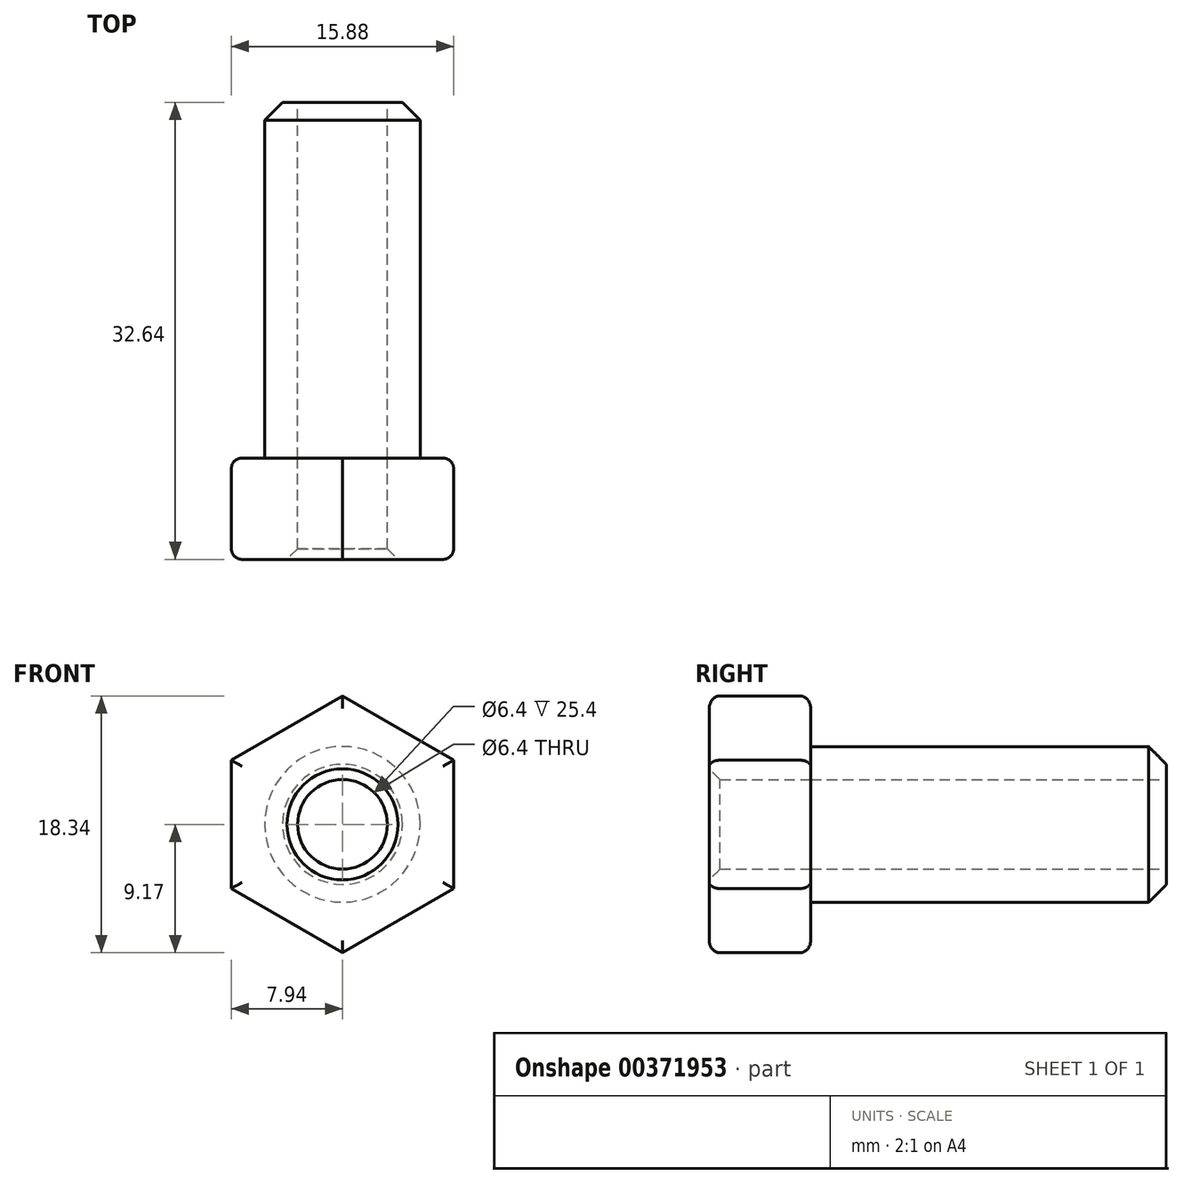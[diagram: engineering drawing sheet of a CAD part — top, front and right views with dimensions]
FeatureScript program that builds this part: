
annotation { "Feature Type Name" : "Feature", "Feature Type Description" : "" }
export const myFeature = defineFeature(function(context is Context, id is Id, definition is map)
    precondition{}
    {
        {
            var Q0;
            Q0=qCreatedBy(makeId("Front.planeOp"),FACE);
            var sketch = newSketch(context, id + "F0", { "sketchPlane" : qUnion([Q0])});
            skCircle(sketch, "E0.cCircle", {"center": v(0, 0) * mm, "radius": 7.94 * mm, "construction": true});
            skLineSegment(sketch, "E0.0", {"start": v(-7.94, -4.58) * mm, "end": v(-7.94, 4.58) * mm});
            skLineSegment(sketch, "E0.1", {"start": v(-7.94, 4.58) * mm, "end": v(0, 9.17) * mm});
            skLineSegment(sketch, "E0.2", {"start": v(0, 9.17) * mm, "end": v(7.94, 4.58) * mm});
            skLineSegment(sketch, "E0.3", {"start": v(7.94, 4.58) * mm, "end": v(7.94, -4.58) * mm});
            skLineSegment(sketch, "E0.4", {"start": v(7.94, -4.58) * mm, "end": v(0, -9.17) * mm});
            skLineSegment(sketch, "E0.5", {"start": v(0, -9.17) * mm, "end": v(-7.94, -4.58) * mm});
            skPoint(sketch, "E0.0.midPoint", {"position": v(-7.94, 0) * mm});
            skSolve(sketch);
        }
        {
            var Q0;
            Q0 = qSketchRegion(id + "F0", true);
            extrude(context, id + "F1", {"entities" : qUnion([Q0]), "depth" : 7.24 * mm});
        }
        {
            var Q0;
            Q0=makeQuery(id+"F1.opExtrude","CAP_FACE",FACE,{"disambiguationData":[OSD([sQuery(id+"F0.wireOp",EDGE,"E0.0"),sQuery(id+"F0.wireOp",EDGE,"E0.1"),sQuery(id+"F0.wireOp",EDGE,"E0.2"),sQuery(id+"F0.wireOp",EDGE,"E0.3"),sQuery(id+"F0.wireOp",EDGE,"E0.4"),sQuery(id+"F0.wireOp",EDGE,"E0.5")])],"isStart":false});
            var Q1;
            Q1=makeQuery(id+"F1.opExtrude","CAP_FACE",FACE,{"disambiguationData":[OSD([sQuery(id+"F0.wireOp",EDGE,"E0.0"),sQuery(id+"F0.wireOp",EDGE,"E0.1"),sQuery(id+"F0.wireOp",EDGE,"E0.2"),sQuery(id+"F0.wireOp",EDGE,"E0.3"),sQuery(id+"F0.wireOp",EDGE,"E0.4"),sQuery(id+"F0.wireOp",EDGE,"E0.5")])],"isStart":true});
            fillet(context, id + "F2", {"entities" : qUnion([Q0, Q1]), "radius" : 0.76 * mm, "tangentPropagation" : true, "allowEdgeOverflow" : false});
        }
        {
            var Q0;
            Q0=makeQuery(id+"F1.opExtrude","CAP_FACE",FACE,{"disambiguationData":[OSD([sQuery(id+"F0.wireOp",EDGE,"E0.0"),sQuery(id+"F0.wireOp",EDGE,"E0.1"),sQuery(id+"F0.wireOp",EDGE,"E0.2"),sQuery(id+"F0.wireOp",EDGE,"E0.3"),sQuery(id+"F0.wireOp",EDGE,"E0.4"),sQuery(id+"F0.wireOp",EDGE,"E0.5")])],"isStart":true});
            var sketch = newSketch(context, id + "F3", { "sketchPlane" : qUnion([Q0])});
            skCircle(sketch, "E1", {"center": v(0, 0) * mm, "radius": 5.56 * mm});
            skSolve(sketch);
        }
        {
            var Q0;
            Q0=makeQuery(id+"F3.imprint","IMPRINT",FACE,{"disambiguationData":[TD([[makeQuery(id+"F3.imprint","IMPRINT",EDGE,{"derivedFrom":sQuery(id+"F3.wireOp",EDGE,"E1")}),1.0]])]});
            var Q1;
            Q1=sQuery(id+"F3.wireOp",EDGE,"E1");
            extrude(context, id + "F4", {"entities" : qUnion([Q0]), "surfaceEntities" : qUnion([Q1]), "depth" : 25.4 * mm});
        }
        {
            var Q0;
            Q0=makeQuery(id+"F4.opExtrude","CAP_EDGE",EDGE,{"disambiguationData":[OSD([sQuery(id+"F3.wireOp",EDGE,"E1")])],"isStart":false});
            chamfer(context, id + "F5", {"entities" : qUnion([Q0]), "width" : 1.27 * mm, "tangentPropagation" : true});
        }
        {
            var Q0;
            Q0=makeQuery(id+"F4.opExtrude","CAP_FACE",FACE,{"disambiguationData":[OSD([sQuery(id+"F3.wireOp",EDGE,"E1")])],"isStart":false});
            var sketch = newSketch(context, id + "F6", { "sketchPlane" : qUnion([Q0])});
            skCircle(sketch, "E2", {"center": v(0, 0) * mm, "radius": 3.2 * mm});
            skSolve(sketch);
        }
        {
            var Q0;
            Q0 = qSketchRegion(id + "F6", true);
            var Q1;
            Q1=makeQuery(id+"F1.opExtrude","CAP_FACE",FACE,{"disambiguationData":[OSD([sQuery(id+"F0.wireOp",EDGE,"E0.0"),sQuery(id+"F0.wireOp",EDGE,"E0.1"),sQuery(id+"F0.wireOp",EDGE,"E0.2"),sQuery(id+"F0.wireOp",EDGE,"E0.3"),sQuery(id+"F0.wireOp",EDGE,"E0.4"),sQuery(id+"F0.wireOp",EDGE,"E0.5")])],"isStart":false});
            extrude(context, id + "F7", {"entities" : qUnion([Q0]), "operationType" : NewBodyOperationType.REMOVE, "oppositeDirection" : true, "endBoundEntityFace" : qUnion([Q1]), "depth" : 50.8 * mm});
        }
        {
            var Q0;
            Q0=makeQuery(id+"F7.boolean.opBoolean","INTERSECT",EDGE,{"derivedFrom":[makeQuery(id+"F1.opExtrude","CAP_FACE",FACE,{"disambiguationData":[OSD([sQuery(id+"F0.wireOp",EDGE,"E0.0"),sQuery(id+"F0.wireOp",EDGE,"E0.1"),sQuery(id+"F0.wireOp",EDGE,"E0.2"),sQuery(id+"F0.wireOp",EDGE,"E0.3"),sQuery(id+"F0.wireOp",EDGE,"E0.4"),sQuery(id+"F0.wireOp",EDGE,"E0.5")])],"isStart":false}),makeQuery(id+"F7.opExtrude","SWEPT_FACE",FACE,{"disambiguationData":[OSD([sQuery(id+"F6.wireOp",EDGE,"E2")])]})]});
            chamfer(context, id + "F8", {"entities" : qUnion([Q0]), "width" : 0.76 * mm, "tangentPropagation" : true});
        }
    });
